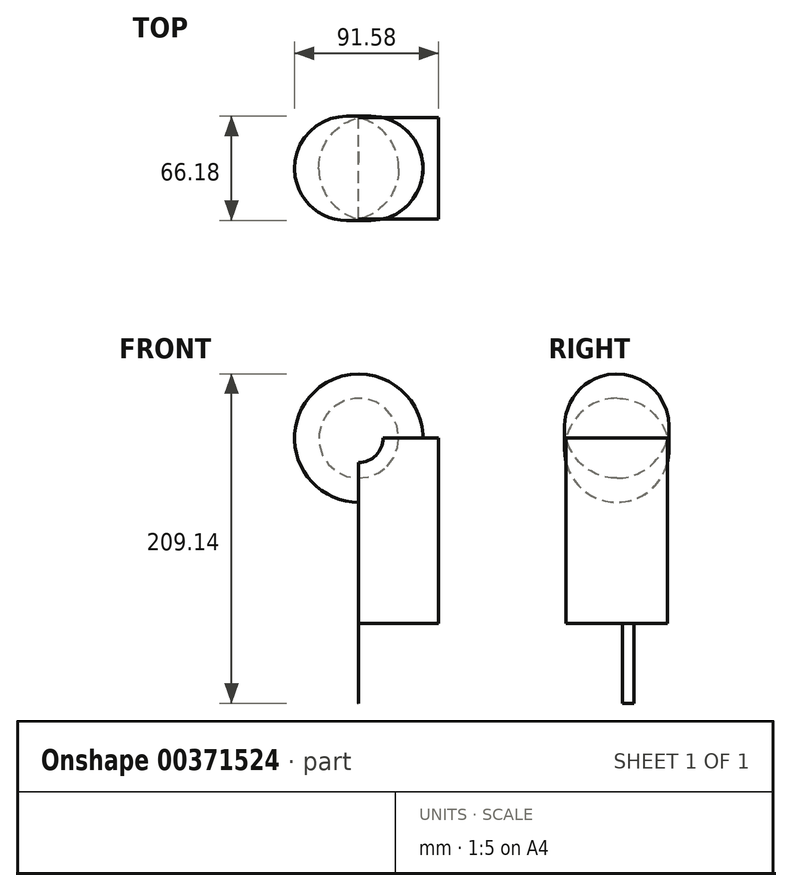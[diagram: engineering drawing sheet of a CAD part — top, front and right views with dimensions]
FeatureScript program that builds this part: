
annotation { "Feature Type Name" : "Feature", "Feature Type Description" : "" }
export const myFeature = defineFeature(function(context is Context, id is Id, definition is map)
    precondition{}
    {
        {
            var Q0;
            Q0=qCreatedBy(makeId("Right.planeOp"),FACE);
            var sketch = newSketch(context, id + "F0", { "sketchPlane" : qUnion([Q0])});
            skLineSegment(sketch, "E0.bottom", {"start": v(-32.18, 58.78) * mm, "end": v(32.18, 58.78) * mm});
            skLineSegment(sketch, "E0.top", {"start": v(-32.18, -58.78) * mm, "end": v(32.18, -58.78) * mm});
            skLineSegment(sketch, "E0.left", {"start": v(-32.18, 58.78) * mm, "end": v(-32.18, -58.78) * mm});
            skLineSegment(sketch, "E0.right", {"start": v(32.18, 58.78) * mm, "end": v(32.18, -58.78) * mm});
            skPoint(sketch, "E0.middle", {"position": v(0, 0) * mm});
            skSolve(sketch);
        }
        {
            var Q0;
            Q0=makeQuery(id+"F0.imprint","IMPRINT",FACE,{"disambiguationData":[TD([[makeQuery(id+"F0.imprint","IMPRINT",EDGE,{"derivedFrom":sQuery(id+"F0.wireOp",EDGE,"E0.bottom")}),-1.0]])]});
            extrude(context, id + "F1", {"entities" : qUnion([Q0]), "endBound" : BoundingType.SYMMETRIC, "depth" : 50.8 * mm});
        }
        {
            var Q0;
            Q0=makeQuery(id+"F1.opExtrude","SWEPT_FACE",FACE,{"disambiguationData":[OSD([sQuery(id+"F0.wireOp",EDGE,"E0.top")])]});
            var sketch = newSketch(context, id + "F2", { "sketchPlane" : qUnion([Q0])});
            skCircle(sketch, "E1", {"center": v(0, -7.19) * mm, "radius": 25.66 * mm});
            skSolve(sketch);
        }
        {
            var Q0;
            {var subQ0=sQuery(id+"F2.wireOp",EDGE,"E1");var subQ1=sQuery(id+"F0.wireOp",EDGE,"E0.top");var subQ8=makeQuery(id+"F1.opExtrude","CAP_EDGE",EDGE,{"disambiguationData":[OSD([subQ1])],"isStart":true});var subQ10=makeQuery(id+"F2.imprint","INTERSECT",VERTEX,{"disambiguationData":[OD(0.0)],"derivedFrom":[subQ8,subQ0]});Q0=makeQuery(id+"F2.imprint","IMPRINT",FACE,{"disambiguationData":[TD([[makeQuery(id+"F2.imprint","IMPRINT",EDGE,{"disambiguationData":[TD([[subQ10,1.0]])],"derivedFrom":subQ0}),1.0]])]});}
            extrude(context, id + "F3", {"entities" : qUnion([Q0]), "operationType" : NewBodyOperationType.ADD, "depth" : 50.8 * mm});
        }
        {
            var Q0;
            Q0=makeQuery(id+"F1.opExtrude","SWEPT_FACE",FACE,{"disambiguationData":[OSD([sQuery(id+"F0.wireOp",EDGE,"E0.bottom")])]});
            var sketch = newSketch(context, id + "F4", { "sketchPlane" : qUnion([Q0])});
            skArc(sketch, "E2", {"start": v(-25.4, 32.18) * mm, "mid": v(-59.06, -20.5) * mm, "end": v(0, 0) * mm});
            skLineSegment(sketch, "E3", {"start": v(0, 0) * mm, "end": v(-25.4, 32.18) * mm});
            skSolve(sketch);
        }
        {
            var Q0;
            {var subQ1=sQuery(id+"F0.wireOp",EDGE,"E0.bottom");var subQ2=makeQuery(id+"F1.opExtrude","CAP_EDGE",EDGE,{"disambiguationData":[OSD([subQ1])],"isStart":true});Q0=makeQuery(id+"F4.imprint","IMPRINT",FACE,{"disambiguationData":[TD([[makeQuery(id+"F4.imprint","IMPRINT",EDGE,{"derivedFrom":subQ2}),1.0]])]});}
            var Q1;
            Q1=makeQuery(id+"F1.opExtrude","CAP_EDGE",EDGE,{"disambiguationData":[OSD([sQuery(id+"F0.wireOp",EDGE,"E0.bottom")])],"isStart":true});
            revolve(context, id + "F5", {"operationType" : NewBodyOperationType.ADD, "entities" : qUnion([Q0]), "axis" : qUnion([Q1]), "revolveType" : RevolveType.FULL});
        }
    });
